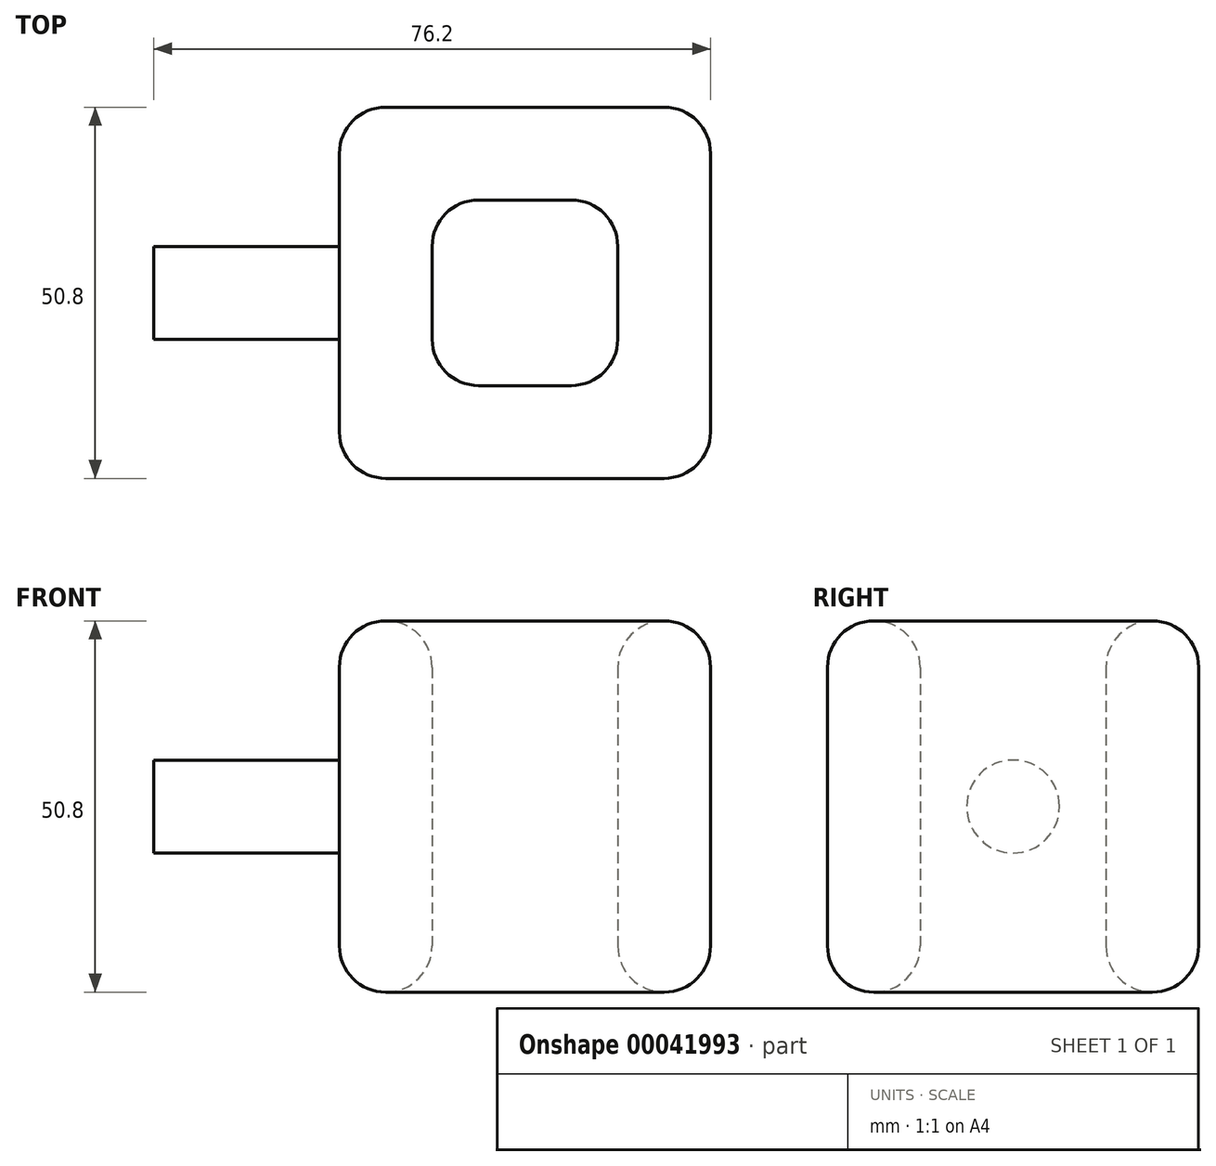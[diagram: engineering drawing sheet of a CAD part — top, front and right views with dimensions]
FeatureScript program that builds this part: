
annotation { "Feature Type Name" : "Feature", "Feature Type Description" : "" }
export const myFeature = defineFeature(function(context is Context, id is Id, definition is map)
    precondition{}
    {
        {
            var Q0;
            Q0=qCreatedBy(makeId("Right.planeOp"),FACE);
            var sketch = newSketch(context, id + "F0", { "sketchPlane" : qUnion([Q0])});
            skLineSegment(sketch, "E0.rect.bottom", {"start": v(25.4, 25.4) * mm, "end": v(-25.4, 25.4) * mm});
            skLineSegment(sketch, "E0.rect.top", {"start": v(25.4, -25.4) * mm, "end": v(-25.4, -25.4) * mm});
            skLineSegment(sketch, "E0.rect.left", {"start": v(25.4, 25.4) * mm, "end": v(25.4, -25.4) * mm});
            skLineSegment(sketch, "E0.rect.right", {"start": v(-25.4, 25.4) * mm, "end": v(-25.4, -25.4) * mm});
            skPoint(sketch, "E0.rect.middle", {"position": v(0, 0) * mm});
            skSolve(sketch);
        }
        {
            var Q0;
            Q0=makeQuery(id+"F0.imprint","IMPRINT",FACE,{"disambiguationData":[TD([[makeQuery(id+"F0.imprint","IMPRINT",EDGE,{"derivedFrom":sQuery(id+"F0.wireOp",EDGE,"E0.rect.bottom")}),1.0]])]});
            extrude(context, id + "F1", {"entities" : qUnion([Q0]), "depth" : 50.8 * mm});
        }
        {
            var Q0;
            Q0=makeQuery(id+"F1.opExtrude","SWEPT_FACE",FACE,{"disambiguationData":[OSD([sQuery(id+"F0.wireOp",EDGE,"E0.rect.bottom")])]});
            var Q1;
            Q1=makeQuery(id+"F1.opExtrude","SWEPT_FACE",FACE,{"disambiguationData":[OSD([sQuery(id+"F0.wireOp",EDGE,"E0.rect.top")])]});
            shell(context, id + "F2", {"entities" : qUnion([Q0, Q1]), "thickness" : 12.7 * mm});
        }
        {
            var Q0;
            Q0=makeQuery(id+"F1.opExtrude","CAP_FACE",FACE,{"disambiguationData":[OSD([sQuery(id+"F0.wireOp",EDGE,"E0.rect.bottom"),sQuery(id+"F0.wireOp",EDGE,"E0.rect.top"),sQuery(id+"F0.wireOp",EDGE,"E0.rect.left"),sQuery(id+"F0.wireOp",EDGE,"E0.rect.right")])],"isStart":true});
            var sketch = newSketch(context, id + "F3", { "sketchPlane" : qUnion([Q0])});
            skCircle(sketch, "E1", {"center": v(0, 0) * mm, "radius": 6.35 * mm});
            skSolve(sketch);
        }
        {
            var Q0;
            Q0=makeQuery(id+"F3.imprint","IMPRINT",FACE,{"disambiguationData":[TD([[makeQuery(id+"F3.imprint","IMPRINT",EDGE,{"derivedFrom":sQuery(id+"F3.wireOp",EDGE,"E1")}),1.0]])]});
            extrude(context, id + "F4", {"entities" : qUnion([Q0]), "operationType" : NewBodyOperationType.ADD, "depth" : 25.4 * mm});
        }
        {
            var Q0;
            Q0=makeQuery(id+"F1.opExtrude","CAP_EDGE",EDGE,{"disambiguationData":[OSD([sQuery(id+"F0.wireOp",EDGE,"E0.rect.right")])],"isStart":false});
            var Q1;
            Q1=makeQuery(id+"F1.opExtrude","CAP_EDGE",EDGE,{"disambiguationData":[OSD([sQuery(id+"F0.wireOp",EDGE,"E0.rect.right")])],"isStart":true});
            var Q2;
            Q2=makeQuery(id+"F1.opExtrude","CAP_EDGE",EDGE,{"disambiguationData":[OSD([sQuery(id+"F0.wireOp",EDGE,"E0.rect.left")])],"isStart":false});
            var Q3;
            Q3=makeQuery(id+"F1.opExtrude","CAP_EDGE",EDGE,{"disambiguationData":[OSD([sQuery(id+"F0.wireOp",EDGE,"E0.rect.left")])],"isStart":true});
            var Q4;
            {var subQ0=sQuery(id+"F0.wireOp",EDGE,"E0.rect.right");Q4=makeQuery(id+"F2.opShell","OFFSET_EDGE",EDGE,{"disambiguationData":[OSD([subQ0]),TDD([makeQuery(id+"F1.opExtrude","CAP_EDGE",EDGE,{"disambiguationData":[OSD([subQ0])],"isStart":true})])]});}
            var Q5;
            {var subQ0=sQuery(id+"F0.wireOp",EDGE,"E0.rect.left");Q5=makeQuery(id+"F2.opShell","OFFSET_EDGE",EDGE,{"disambiguationData":[OSD([subQ0]),TDD([makeQuery(id+"F1.opExtrude","CAP_EDGE",EDGE,{"disambiguationData":[OSD([subQ0])],"isStart":false})])]});}
            var Q6;
            {var subQ0=sQuery(id+"F0.wireOp",EDGE,"E0.rect.left");Q6=makeQuery(id+"F2.opShell","OFFSET_EDGE",EDGE,{"disambiguationData":[OSD([subQ0]),TDD([makeQuery(id+"F1.opExtrude","CAP_EDGE",EDGE,{"disambiguationData":[OSD([subQ0])],"isStart":true})])]});}
            var Q7;
            {var subQ0=sQuery(id+"F0.wireOp",EDGE,"E0.rect.right");Q7=makeQuery(id+"F2.opShell","OFFSET_EDGE",EDGE,{"disambiguationData":[OSD([subQ0]),TDD([makeQuery(id+"F1.opExtrude","CAP_EDGE",EDGE,{"disambiguationData":[OSD([subQ0])],"isStart":false})])]});}
            var Q8;
            Q8=makeQuery(id+"F1.opExtrude","SWEPT_FACE",FACE,{"disambiguationData":[OSD([sQuery(id+"F0.wireOp",EDGE,"E0.rect.bottom")])]});
            var Q9;
            Q9=makeQuery(id+"F1.opExtrude","SWEPT_FACE",FACE,{"disambiguationData":[OSD([sQuery(id+"F0.wireOp",EDGE,"E0.rect.top")])]});
            fillet(context, id + "F5", {"entities" : qUnion([Q0, Q1, Q2, Q3, Q4, Q5, Q6, Q7, Q8, Q9]), "radius" : 6.35 * mm, "tangentPropagation" : true, "allowEdgeOverflow" : false});
        }
        {
            var Q0;
            Q0=qCreatedBy(makeId("Top.planeOp"),FACE);
            var sketch = newSketch(context, id + "F6", { "sketchPlane" : qUnion([Q0])});
            skPoint(sketch, "E2", {"position": v(25.4, 0) * mm});
            skLineSegment(sketch, "E3", {"start": v(25.4, 0) * mm, "end": v(25.4, 12.7) * mm});
            skSolve(sketch);
        }
    });
